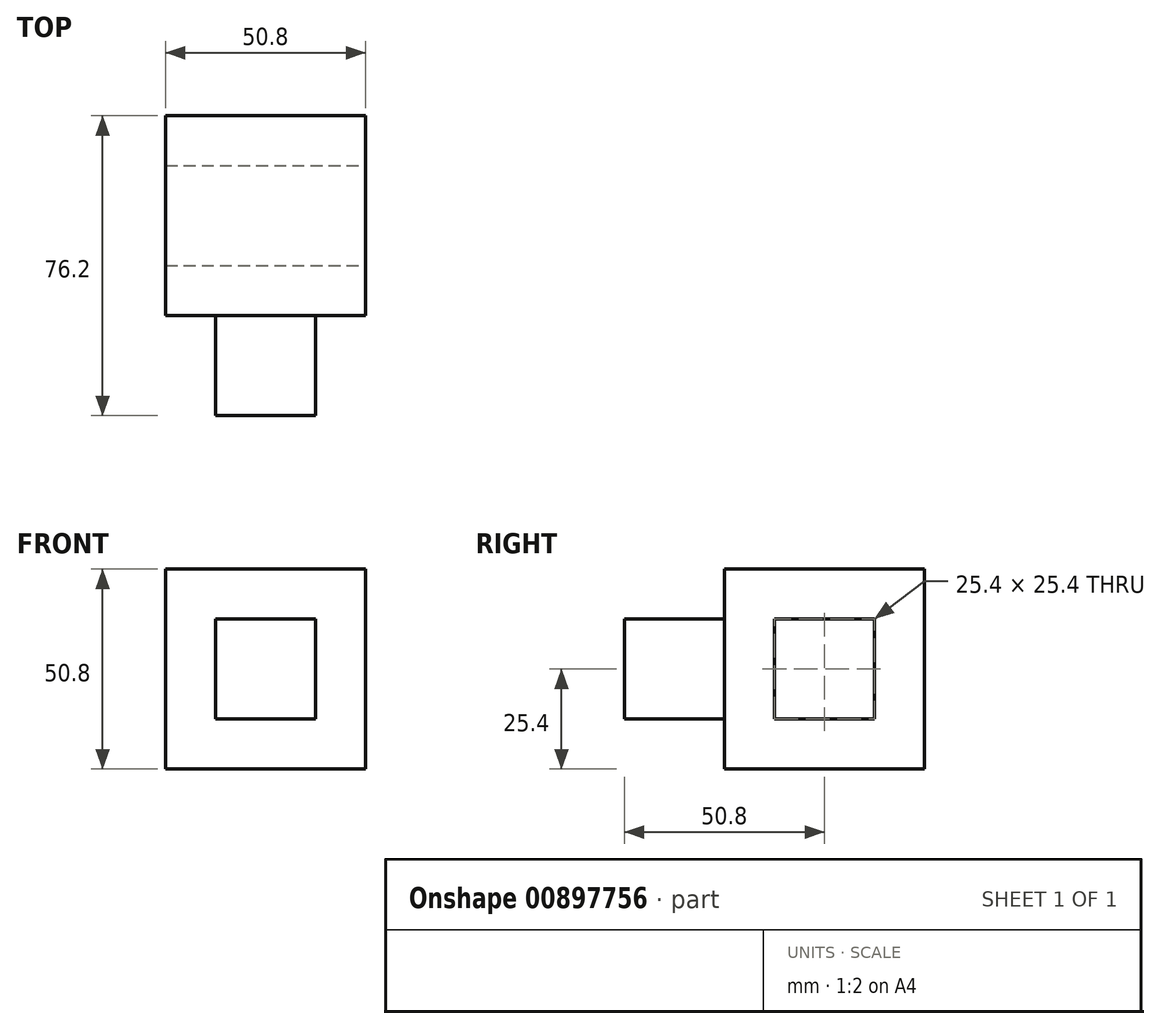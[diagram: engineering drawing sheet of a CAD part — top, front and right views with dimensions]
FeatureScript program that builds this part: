
annotation { "Feature Type Name" : "Feature", "Feature Type Description" : "" }
export const myFeature = defineFeature(function(context is Context, id is Id, definition is map)
    precondition{}
    {
        {
            var Q0;
            Q0=qCreatedBy(makeId("Front.planeOp"),FACE);
            var sketch = newSketch(context, id + "F0", { "sketchPlane" : qUnion([Q0])});
            skLineSegment(sketch, "E0.bottom", {"start": v(25.4, 25.4) * mm, "end": v(-25.4, 25.4) * mm});
            skLineSegment(sketch, "E0.top", {"start": v(25.4, -25.4) * mm, "end": v(-25.4, -25.4) * mm});
            skLineSegment(sketch, "E0.left", {"start": v(25.4, 25.4) * mm, "end": v(25.4, -25.4) * mm});
            skLineSegment(sketch, "E0.right", {"start": v(-25.4, 25.4) * mm, "end": v(-25.4, -25.4) * mm});
            skPoint(sketch, "E0.middle", {"position": v(0, 0) * mm});
            skSolve(sketch);
        }
        {
            var Q0;
            Q0=makeQuery(id+"F0.imprint","IMPRINT",FACE,{"disambiguationData":[TD([[makeQuery(id+"F0.imprint","IMPRINT",EDGE,{"derivedFrom":sQuery(id+"F0.wireOp",EDGE,"E0.bottom")}),1.0]])]});
            extrude(context, id + "F1", {"entities" : qUnion([Q0]), "depth" : 50.8 * mm, "offsetDistance" : 25.4 * mm});
        }
        {
            var Q0;
            Q0=makeQuery(id+"F1.opExtrude","CAP_FACE",FACE,{"disambiguationData":[OSD([sQuery(id+"F0.wireOp",EDGE,"E0.bottom"),sQuery(id+"F0.wireOp",EDGE,"E0.top"),sQuery(id+"F0.wireOp",EDGE,"E0.left"),sQuery(id+"F0.wireOp",EDGE,"E0.right")])],"isStart":false});
            var sketch = newSketch(context, id + "F2", { "sketchPlane" : qUnion([Q0])});
            skLineSegment(sketch, "E1.bottom", {"start": v(12.7, 12.7) * mm, "end": v(-12.7, 12.7) * mm});
            skLineSegment(sketch, "E1.top", {"start": v(12.7, -12.7) * mm, "end": v(-12.7, -12.7) * mm});
            skLineSegment(sketch, "E1.left", {"start": v(12.7, 12.7) * mm, "end": v(12.7, -12.7) * mm});
            skLineSegment(sketch, "E1.right", {"start": v(-12.7, 12.7) * mm, "end": v(-12.7, -12.7) * mm});
            skPoint(sketch, "E1.middle", {"position": v(0, 0) * mm});
            skSolve(sketch);
        }
        {
            var Q0;
            Q0=makeQuery(id+"F2.imprint","IMPRINT",FACE,{"disambiguationData":[TD([[makeQuery(id+"F2.imprint","IMPRINT",EDGE,{"derivedFrom":sQuery(id+"F2.wireOp",EDGE,"E1.bottom")}),1.0]])]});
            extrude(context, id + "F3", {"entities" : qUnion([Q0]), "operationType" : NewBodyOperationType.ADD, "depth" : 25.4 * mm, "offsetDistance" : 25.4 * mm});
        }
        {
            var Q0;
            Q0=makeQuery(id+"F1.opExtrude","SWEPT_FACE",FACE,{"disambiguationData":[OSD([sQuery(id+"F0.wireOp",EDGE,"E0.left")])]});
            var sketch = newSketch(context, id + "F4", { "sketchPlane" : qUnion([Q0])});
            skLineSegment(sketch, "E2.bottom", {"start": v(-12.7, -12.7) * mm, "end": v(-38.1, -12.7) * mm});
            skLineSegment(sketch, "E2.top", {"start": v(-12.7, 12.7) * mm, "end": v(-38.1, 12.7) * mm});
            skLineSegment(sketch, "E2.left", {"start": v(-12.7, -12.7) * mm, "end": v(-12.7, 12.7) * mm});
            skLineSegment(sketch, "E2.right", {"start": v(-38.1, -12.7) * mm, "end": v(-38.1, 12.7) * mm});
            skSolve(sketch);
        }
        {
            var Q0;
            Q0=makeQuery(id+"F4.imprint","IMPRINT",FACE,{"disambiguationData":[TD([[makeQuery(id+"F4.imprint","IMPRINT",EDGE,{"derivedFrom":sQuery(id+"F4.wireOp",EDGE,"E2.bottom")}),-1.0]])]});
            extrude(context, id + "F5", {"entities" : qUnion([Q0]), "operationType" : NewBodyOperationType.REMOVE, "endBound" : BoundingType.THROUGH_ALL, "oppositeDirection" : true, "depth" : 25.4 * mm, "offsetDistance" : 25.4 * mm});
        }
    });
